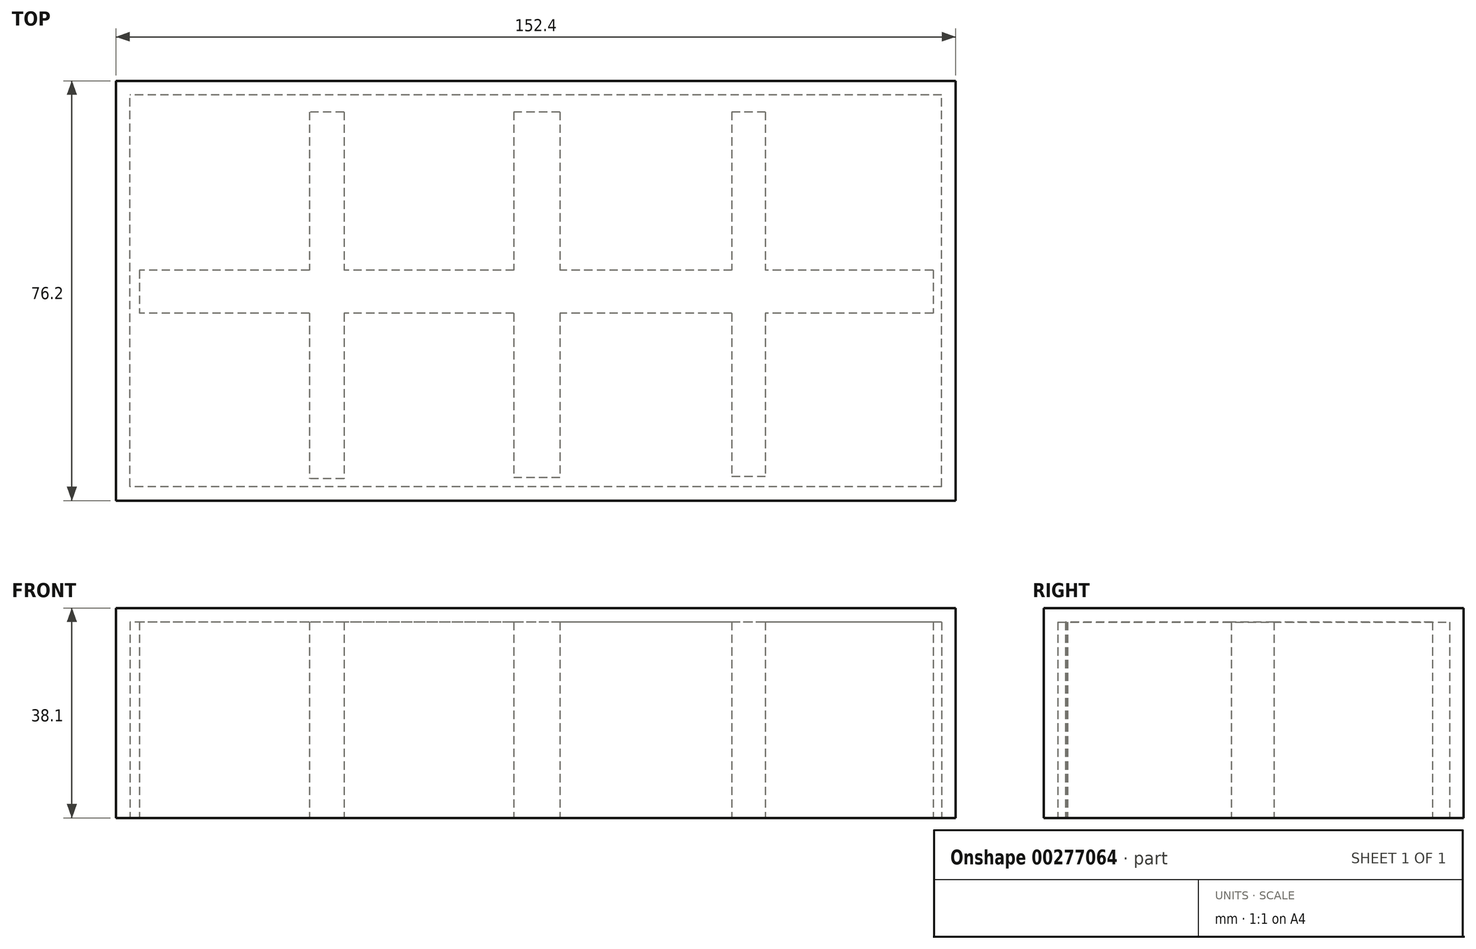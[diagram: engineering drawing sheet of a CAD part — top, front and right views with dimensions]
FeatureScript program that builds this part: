
annotation { "Feature Type Name" : "Feature", "Feature Type Description" : "" }
export const myFeature = defineFeature(function(context is Context, id is Id, definition is map)
    precondition{}
    {
        {
            var Q0;
            Q0=qCreatedBy(makeId("Top.planeOp"),FACE);
            var sketch = newSketch(context, id + "F0", { "sketchPlane" : qUnion([Q0])});
            skLineSegment(sketch, "E0.bottom", {"start": v(76.2, -38.1) * mm, "end": v(-76.2, -38.1) * mm});
            skLineSegment(sketch, "E0.top", {"start": v(76.2, 38.1) * mm, "end": v(-76.2, 38.1) * mm});
            skLineSegment(sketch, "E0.left", {"start": v(76.2, -38.1) * mm, "end": v(76.2, 38.1) * mm});
            skLineSegment(sketch, "E0.right", {"start": v(-76.2, -38.1) * mm, "end": v(-76.2, 38.1) * mm});
            skPoint(sketch, "E0.middle", {"position": v(0, 0) * mm});
            skSolve(sketch);
        }
        {
            var Q0;
            Q0 = qSketchRegion(id + "F0", true);
            extrude(context, id + "F1", {"entities" : qUnion([Q0]), "depth" : 38.1 * mm});
        }
        {
            var Q0;
            Q0=makeQuery(id+"F1.opExtrude","CAP_FACE",FACE,{"disambiguationData":[OSD([sQuery(id+"F0.wireOp",EDGE,"E0.bottom"),sQuery(id+"F0.wireOp",EDGE,"E0.top"),sQuery(id+"F0.wireOp",EDGE,"E0.left"),sQuery(id+"F0.wireOp",EDGE,"E0.right")])],"isStart":true});
            shell(context, id + "F2", {"entities" : qUnion([Q0]), "thickness" : 2.54 * mm});
        }
        {
            var Q0;
            Q0=qCreatedBy(makeId("Top.planeOp"),FACE);
            var sketch = newSketch(context, id + "F3", { "sketchPlane" : qUnion([Q0])});
            skLineSegment(sketch, "E1.bottom", {"start": v(-71.92, -4.1) * mm, "end": v(72.11, -4.1) * mm});
            skLineSegment(sketch, "E1.top", {"start": v(-71.92, 3.71) * mm, "end": v(72.11, 3.71) * mm});
            skLineSegment(sketch, "E1.left", {"start": v(-71.92, -4.1) * mm, "end": v(-71.92, 3.71) * mm});
            skLineSegment(sketch, "E1.right", {"start": v(72.11, -4.1) * mm, "end": v(72.11, 3.71) * mm});
            skLineSegment(sketch, "E2.bottom", {"start": v(-41.1, -34.15) * mm, "end": v(-34.82, -34.15) * mm});
            skLineSegment(sketch, "E2.top", {"start": v(-41.1, 32.44) * mm, "end": v(-34.82, 32.44) * mm});
            skLineSegment(sketch, "E2.left", {"start": v(-41.1, -34.15) * mm, "end": v(-41.1, 32.44) * mm});
            skLineSegment(sketch, "E2.right", {"start": v(-34.82, -34.15) * mm, "end": v(-34.82, 32.44) * mm});
            skLineSegment(sketch, "E3.bottom", {"start": v(-4, -33.96) * mm, "end": v(4.38, -33.96) * mm});
            skLineSegment(sketch, "E3.top", {"start": v(-4, 32.44) * mm, "end": v(4.38, 32.44) * mm});
            skLineSegment(sketch, "E3.left", {"start": v(-4, -33.96) * mm, "end": v(-4, 32.44) * mm});
            skLineSegment(sketch, "E3.right", {"start": v(4.38, -33.96) * mm, "end": v(4.38, 32.44) * mm});
            skLineSegment(sketch, "E4.bottom", {"start": v(35.58, -33.77) * mm, "end": v(41.67, -33.77) * mm});
            skLineSegment(sketch, "E4.top", {"start": v(35.58, 32.44) * mm, "end": v(41.67, 32.44) * mm});
            skLineSegment(sketch, "E4.left", {"start": v(35.58, -33.77) * mm, "end": v(35.58, 32.44) * mm});
            skLineSegment(sketch, "E4.right", {"start": v(41.67, -33.77) * mm, "end": v(41.67, 32.44) * mm});
            skSolve(sketch);
        }
        {
            var Q0;
            Q0 = qSketchRegion(id + "F3", true);
            extrude(context, id + "F4", {"entities" : qUnion([Q0]), "operationType" : NewBodyOperationType.ADD, "depth" : 38.1 * mm});
        }
    });
